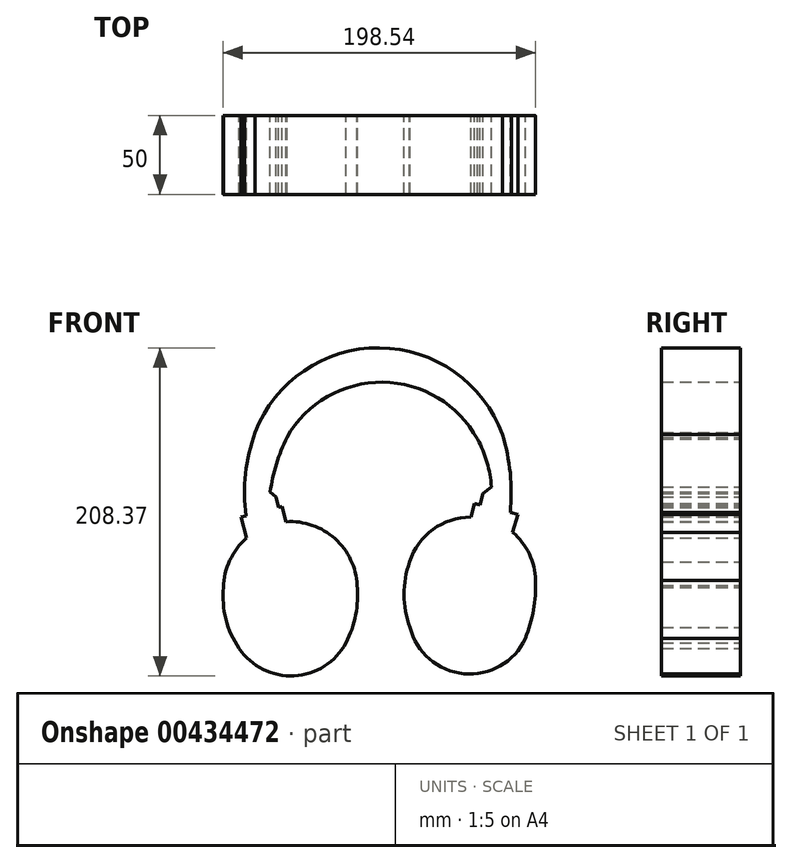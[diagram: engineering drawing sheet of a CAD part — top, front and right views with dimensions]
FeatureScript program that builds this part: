
annotation { "Feature Type Name" : "Feature", "Feature Type Description" : "" }
export const myFeature = defineFeature(function(context is Context, id is Id, definition is map)
    precondition{}
    {
        {
            var Q0;
            Q0=qCreatedBy(makeId("Front.planeOp"),FACE);
            var sketch = newSketch(context, id + "F0", { "sketchPlane" : qUnion([Q0])});
            skArc(sketch, "E0", {"start": v(-15.28, -46.68) * mm, "mid": v(-29.37, -17.02) * mm, "end": v(-60.4, -6.3) * mm});
            skLineSegment(sketch, "E1", {"start": v(-89.07, -3.4) * mm, "end": v(-85.6, -16.7) * mm});
            skLineSegment(sketch, "E2", {"start": v(-62.95, 3.43) * mm, "end": v(-60.38, -6.4) * mm});
            skLineSegment(sketch, "E3", {"start": v(-89.07, -3.4) * mm, "end": v(-85.82, -2.55) * mm});
            skArc(sketch, "E4.trimOffspring", {"start": v(-85.6, -16.7) * mm, "mid": v(-96.18, -30.83) * mm, "end": v(-100.09, -48.05) * mm});
            skArc(sketch, "E5", {"start": v(98.06, -43.6) * mm, "mid": v(94.1, -26.74) * mm, "end": v(83.51, -13.03) * mm});
            skArc(sketch, "E6", {"start": v(18.36, -73.43) * mm, "mid": v(52.47, -102.85) * mm, "end": v(91.56, -80.48) * mm});
            skArc(sketch, "E7", {"start": v(18.09, -31.68) * mm, "mid": v(14.5, -52.58) * mm, "end": v(18.36, -73.43) * mm});
            skArc(sketch, "E8", {"start": v(91.56, -80.48) * mm, "mid": v(96.73, -62.38) * mm, "end": v(98.06, -43.6) * mm});
            skArc(sketch, "E9", {"start": v(-90.15, -86.76) * mm, "mid": v(-55.27, -104.16) * mm, "end": v(-22.37, -83.23) * mm});
            skArc(sketch, "E10", {"start": v(-100.09, -48.05) * mm, "mid": v(-98.65, -68.31) * mm, "end": v(-90.15, -86.76) * mm});
            skArc(sketch, "E11", {"start": v(-22.37, -83.23) * mm, "mid": v(-16.24, -65.46) * mm, "end": v(-15.28, -46.68) * mm});
            skLineSegment(sketch, "E12", {"start": v(59.19, 5.37) * mm, "end": v(56.97, -3.36) * mm});
            skLineSegment(sketch, "E13", {"start": v(86.9, -1.65) * mm, "end": v(83.51, -13.03) * mm});
            skLineSegment(sketch, "E14", {"start": v(59.19, 5.37) * mm, "end": v(62.8, 4.46) * mm});
            skArc(sketch, "E15.trimOffspring", {"start": v(56.97, -3.36) * mm, "mid": v(32.94, -11.22) * mm, "end": v(18.09, -31.68) * mm});
            skArc(sketch, "E16", {"start": v(76.95, 49) * mm, "mid": v(-1.1, 104.15) * mm, "end": v(-80.05, 50.3) * mm});
            skArc(sketch, "E17", {"start": v(-80.05, 50.3) * mm, "mid": v(-86.15, 24.22) * mm, "end": v(-85.82, -2.55) * mm});
            skArc(sketch, "E18", {"start": v(81.95, -0.4) * mm, "mid": v(81.95, 24.56) * mm, "end": v(76.95, 49) * mm});
            skArc(sketch, "E19", {"start": v(61.08, 46.18) * mm, "mid": v(0.93, 82.33) * mm, "end": v(-59.9, 47.36) * mm});
            skArc(sketch, "E20", {"start": v(-59.9, 47.36) * mm, "mid": v(-66.54, 30.36) * mm, "end": v(-70.54, 12.56) * mm});
            skArc(sketch, "E21", {"start": v(69.92, 15.77) * mm, "mid": v(67.28, 31.5) * mm, "end": v(61.08, 46.18) * mm});
            skLineSegment(sketch, "E22", {"start": v(69.92, 15.77) * mm, "end": v(64.6, 11.57) * mm});
            skLineSegment(sketch, "E23", {"start": v(64.6, 11.57) * mm, "end": v(62.8, 4.46) * mm});
            skLineSegment(sketch, "E24", {"start": v(-70.54, 12.56) * mm, "end": v(-66.82, 9.34) * mm});
            skLineSegment(sketch, "E25", {"start": v(-66.82, 9.34) * mm, "end": v(-65.13, 2.86) * mm});
            skLineSegment(sketch, "E26.trimOffspring", {"start": v(-65.13, 2.86) * mm, "end": v(-62.95, 3.43) * mm});
            skLineSegment(sketch, "E27.trimOffspring", {"start": v(81.95, -0.4) * mm, "end": v(86.9, -1.65) * mm});
            skSolve(sketch);
        }
        {
            var Q0;
            Q0 = qSketchRegion(id + "F0", true);
            extrude(context, id + "F1", {"entities" : qUnion([Q0]), "depth" : 50 * mm});
        }
    });
